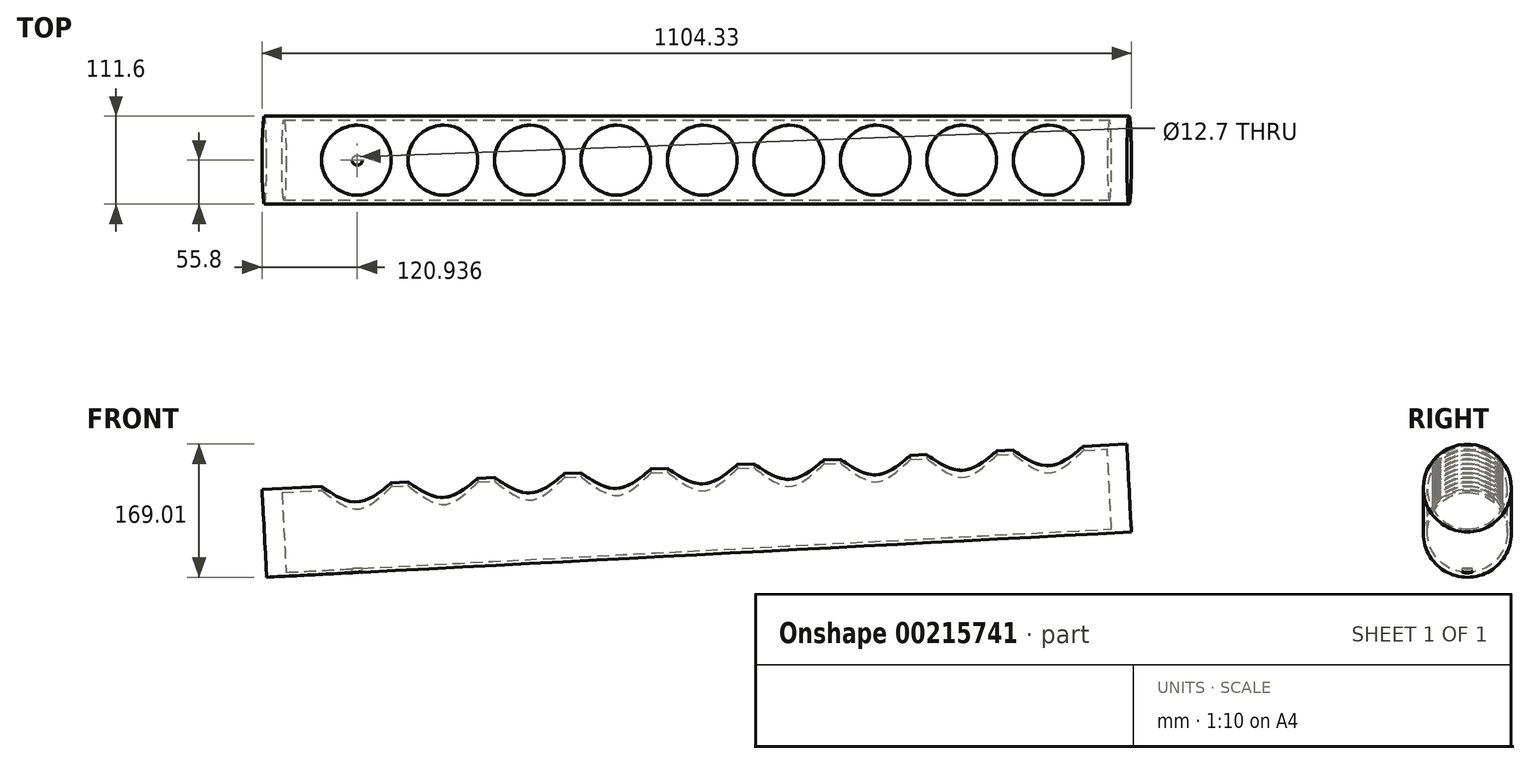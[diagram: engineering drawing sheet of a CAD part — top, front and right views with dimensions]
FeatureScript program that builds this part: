
annotation { "Feature Type Name" : "Feature", "Feature Type Description" : "" }
export const myFeature = defineFeature(function(context is Context, id is Id, definition is map)
    precondition{}
    {
        {
            var Q0;
            Q0=qCreatedBy(makeId("Right.planeOp"),FACE);
            var sketch = newSketch(context, id + "F0", { "sketchPlane" : qUnion([Q0])});
            skCircle(sketch, "E0", {"center": v(0, 0) * mm, "radius": 50.8 * mm});
            skCircle(sketch, "E1.0", {"center": v(0, 0) * mm, "radius": 55.8 * mm});
            skLineSegment(sketch, "E2", {"start": v(-50.8, 0) * mm, "end": v(50.8, 0) * mm, "construction": true});
            skSolve(sketch);
        }
        {
            var Q0;
            Q0=qSketchRegion(id+"F0",true);
            extrude(context, id + "F1", {"entities" : qUnion([Q0]), "oppositeDirection" : true, "depth" : 1100 * mm});
        }
        {
            var Q0;
            Q0=qCreatedBy(makeId("Right.planeOp"),FACE);
            var sketch = newSketch(context, id + "F2", { "sketchPlane" : qUnion([Q0])});
            skLineSegment(sketch, "E3", {"start": v(-70.21, 0) * mm, "end": v(69.9, 0) * mm, "construction": true});
            skSolve(sketch);
        }
        {
            var Q0;
            Q0=qCreatedBy(makeId("Top.planeOp"),FACE);
            var sketch = newSketch(context, id + "F3", { "sketchPlane" : qUnion([Q0])});
            skCircle(sketch, "E4", {"center": v(-100, 0) * mm, "radius": 44.45 * mm});
            skCircle(sketch, "E5.1.0.0", {"center": v(-210, 0) * mm, "radius": 44.45 * mm});
            skCircle(sketch, "E5.2.0.0", {"center": v(-320, 0) * mm, "radius": 44.45 * mm});
            skCircle(sketch, "E5.3.0.0", {"center": v(-430, 0) * mm, "radius": 44.45 * mm});
            skCircle(sketch, "E5.4.0.0", {"center": v(-540, 0) * mm, "radius": 44.45 * mm});
            skCircle(sketch, "E5.5.0.0", {"center": v(-650, 0) * mm, "radius": 44.45 * mm});
            skCircle(sketch, "E5.6.0.0", {"center": v(-760, 0) * mm, "radius": 44.45 * mm});
            skCircle(sketch, "E5.7.0.0", {"center": v(-870, 0) * mm, "radius": 44.45 * mm});
            skCircle(sketch, "E5.8.0.0", {"center": v(-980, 0) * mm, "radius": 44.45 * mm});
            skLineSegment(sketch, "E5.direction1", {"start": v(-100, 0) * mm, "end": v(-210, 0) * mm, "construction": true});
            skSolve(sketch);
        }
        {
            var Q0;
            Q0=qSketchRegion(id+"F3",true);
            extrude(context, id + "F4", {"entities" : qUnion([Q0]), "operationType" : NewBodyOperationType.REMOVE, "endBound" : BoundingType.THROUGH_ALL, "depth" : 25 * mm});
        }
        {
            var Q0;
            Q0=makeQuery(id+"F1.opExtrude","SWEPT_BODY",BODY,{"disambiguationData":[OSD([sQuery(id+"F0.wireOp",EDGE,"E0"),sQuery(id+"F0.wireOp",EDGE,"E1.0")])]});
            var Q1;
            Q1=sQuery(id+"F2.wireOp",EDGE,"E3");
            transform(context, id + "F5", {"entities" : qUnion([Q0]), "transformType" : TransformType.ROTATION, "transformAxis" : qUnion([Q1]), "angle" : 3 * degree, "oppositeDirection" : true, "makeCopy" : false});
        }
        {
            var Q0;
            Q0=makeQuery(id+"F1.opExtrude","CAP_FACE",FACE,{"disambiguationData":[OSD([sQuery(id+"F0.wireOp",EDGE,"E0"),sQuery(id+"F0.wireOp",EDGE,"E1.0")])],"isStart":false});
            var sketch = newSketch(context, id + "F6", { "sketchPlane" : qUnion([Q0])});
            skCircle(sketch, "E6", {"center": v(0, 0) * mm, "radius": 54.33 * mm});
            skSolve(sketch);
        }
        {
            var Q0;
            Q0 = qSketchRegion(id + "F6", true);
            extrude(context, id + "F7", {"entities" : qUnion([Q0]), "operationType" : NewBodyOperationType.ADD, "oppositeDirection" : true, "depth" : 25 * mm});
        }
        {
            var Q0;
            Q0=makeQuery(id+"F1.opExtrude","CAP_FACE",FACE,{"disambiguationData":[OSD([sQuery(id+"F0.wireOp",EDGE,"E0"),sQuery(id+"F0.wireOp",EDGE,"E1.0")])],"isStart":true});
            var sketch = newSketch(context, id + "F8", { "sketchPlane" : qUnion([Q0])});
            skCircle(sketch, "E7", {"center": v(0, 0) * mm, "radius": 53.8 * mm});
            skSolve(sketch);
        }
        {
            var Q0;
            Q0 = qSketchRegion(id + "F8", true);
            extrude(context, id + "F9", {"entities" : qUnion([Q0]), "operationType" : NewBodyOperationType.ADD, "oppositeDirection" : true, "depth" : 25 * mm});
        }
        {
            var Q0;
            Q0=qCreatedBy(makeId("Top.planeOp"),FACE);
            var sketch = newSketch(context, id + "F10", { "sketchPlane" : qUnion([Q0])});
            skCircle(sketch, "E8", {"center": v(-980.47, 0) * mm, "radius": 6.35 * mm});
            skSolve(sketch);
        }
        {
            var Q0;
            Q0 = qSketchRegion(id + "F10", true);
            extrude(context, id + "F11", {"entities" : qUnion([Q0]), "operationType" : NewBodyOperationType.REMOVE, "endBound" : BoundingType.THROUGH_ALL, "oppositeDirection" : true, "depth" : 25 * mm});
        }
    });
